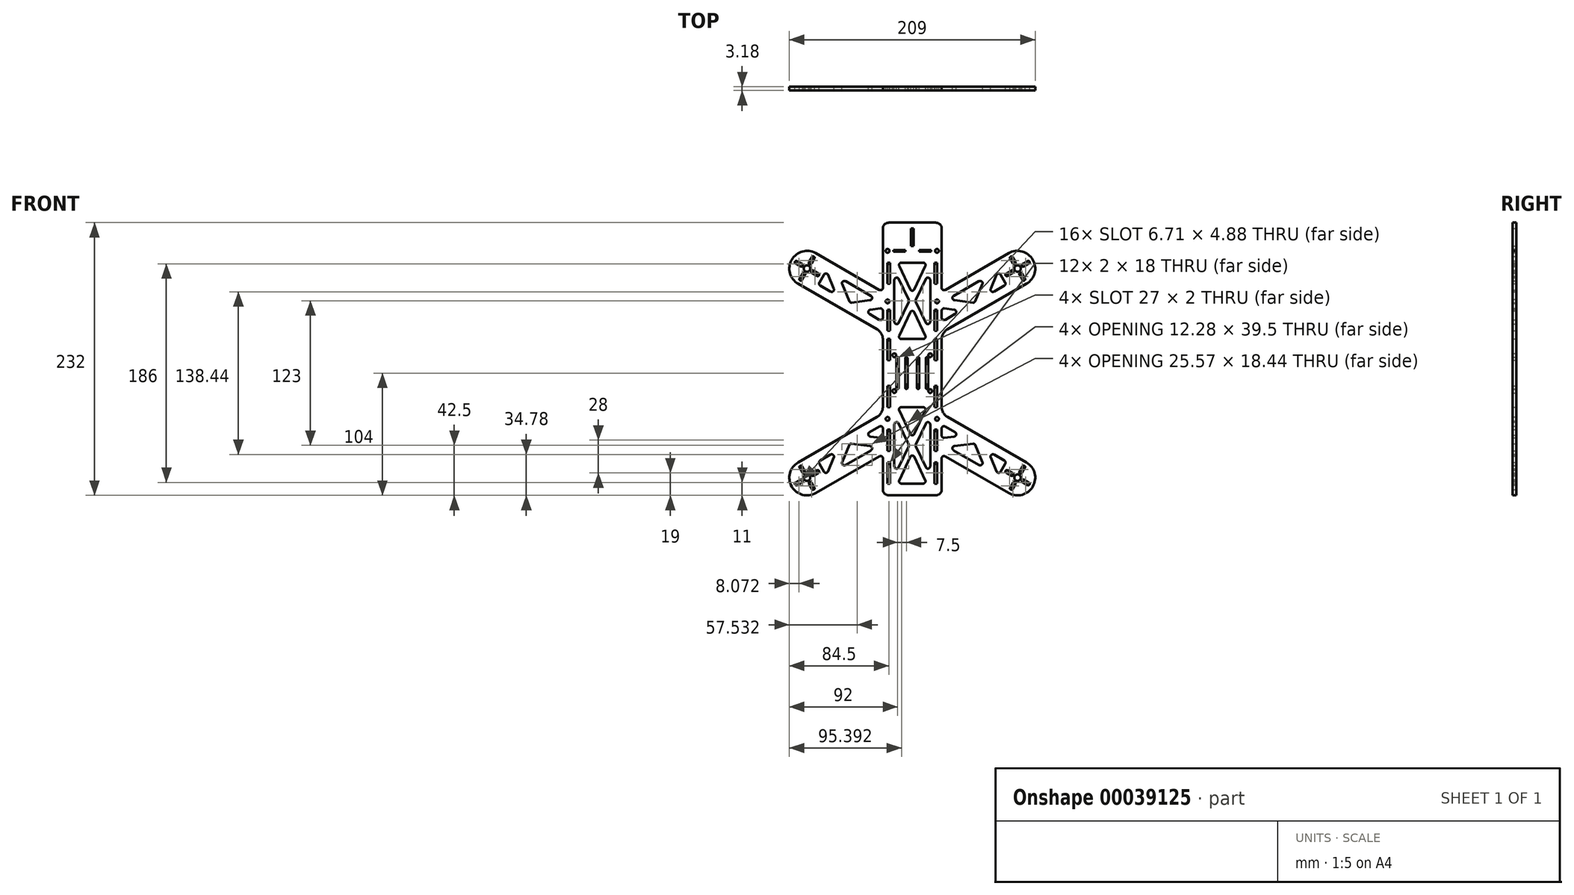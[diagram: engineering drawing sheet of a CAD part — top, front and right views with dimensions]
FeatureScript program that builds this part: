
annotation { "Feature Type Name" : "Feature", "Feature Type Description" : "" }
export const myFeature = defineFeature(function(context is Context, id is Id, definition is map)
    precondition{}
    {
        {
            var Q0;
            Q0=qCreatedBy(makeId("Front.planeOp"),FACE);
            var sketch = newSketch(context, id + "F0", { "sketchPlane" : qUnion([Q0])});
            skArc(sketch, "E0", {"start": v(13.5, 0.5) * mm, "mid": v(12.5, 1.5) * mm, "end": v(11.5, 0.5) * mm});
            skLineSegment(sketch, "E1", {"start": v(13.5, 0.5) * mm, "end": v(13.5, -24.5) * mm});
            skArc(sketch, "E2", {"start": v(11.5, -24.5) * mm, "mid": v(12.5, -25.5) * mm, "end": v(13.5, -24.5) * mm});
            skLineSegment(sketch, "E3", {"start": v(11.5, 0.5) * mm, "end": v(11.5, -24.5) * mm});
            skArc(sketch, "E4", {"start": v(6, 0.5) * mm, "mid": v(5, 1.5) * mm, "end": v(4, 0.5) * mm});
            skLineSegment(sketch, "E5", {"start": v(6, 0.5) * mm, "end": v(6, -24.5) * mm});
            skArc(sketch, "E6", {"start": v(4, -24.5) * mm, "mid": v(5, -25.5) * mm, "end": v(6, -24.5) * mm});
            skLineSegment(sketch, "E7", {"start": v(4, 0.5) * mm, "end": v(4, -24.5) * mm});
            skLineSegment(sketch, "E8", {"start": v(6, 91.25) * mm, "end": v(6, 92.75) * mm});
            skLineSegment(sketch, "E9", {"start": v(6, 92.75) * mm, "end": v(16, 92.75) * mm});
            skLineSegment(sketch, "E10", {"start": v(16, 92.75) * mm, "end": v(16, 91.25) * mm});
            skLineSegment(sketch, "E11", {"start": v(6, 91.25) * mm, "end": v(16, 91.25) * mm});
            skCircle(sketch, "E12", {"center": v(-21, -51) * mm, "radius": 1.6 * mm});
            skCircle(sketch, "E13", {"center": v(-21, 49) * mm, "radius": 1.6 * mm});
            skCircle(sketch, "E14", {"center": v(-21, 92) * mm, "radius": 1.6 * mm});
            skCircle(sketch, "E15", {"center": v(15.25, -27.25) * mm, "radius": 1.6 * mm});
            skCircle(sketch, "E16", {"center": v(-15.25, 3.25) * mm, "radius": 1.6 * mm});
            skCircle(sketch, "E17", {"center": v(-89.5, -101) * mm, "radius": 2.75 * mm});
            skArc(sketch, "E18", {"start": v(-85.34, -97.21) * mm, "mid": v(-85.78, -98.85) * mm, "end": v(-84.14, -99.29) * mm});
            skLineSegment(sketch, "E19", {"start": v(-85.34, -97.21) * mm, "end": v(-81, -94.71) * mm});
            skArc(sketch, "E20", {"start": v(-79.8, -96.79) * mm, "mid": v(-79.37, -95.15) * mm, "end": v(-81, -94.71) * mm});
            skLineSegment(sketch, "E21", {"start": v(-84.14, -99.29) * mm, "end": v(-79.8, -96.79) * mm});
            skArc(sketch, "E22", {"start": v(-85.71, -105.16) * mm, "mid": v(-87.35, -104.72) * mm, "end": v(-87.79, -106.36) * mm});
            skLineSegment(sketch, "E23", {"start": v(-85.71, -105.16) * mm, "end": v(-83.21, -109.5) * mm});
            skArc(sketch, "E24", {"start": v(-85.29, -110.7) * mm, "mid": v(-83.65, -111.13) * mm, "end": v(-83.21, -109.5) * mm});
            skLineSegment(sketch, "E25", {"start": v(-87.79, -106.36) * mm, "end": v(-85.29, -110.7) * mm});
            skArc(sketch, "E26", {"start": v(-93.66, -104.79) * mm, "mid": v(-93.22, -103.15) * mm, "end": v(-94.86, -102.71) * mm});
            skLineSegment(sketch, "E27", {"start": v(-93.66, -104.79) * mm, "end": v(-98, -107.29) * mm});
            skArc(sketch, "E28", {"start": v(-99.2, -105.21) * mm, "mid": v(-99.63, -106.85) * mm, "end": v(-98, -107.29) * mm});
            skLineSegment(sketch, "E29", {"start": v(-94.86, -102.71) * mm, "end": v(-99.2, -105.21) * mm});
            skArc(sketch, "E30", {"start": v(-93.29, -96.84) * mm, "mid": v(-91.65, -97.28) * mm, "end": v(-91.21, -95.64) * mm});
            skLineSegment(sketch, "E31", {"start": v(-93.29, -96.84) * mm, "end": v(-95.79, -92.5) * mm});
            skArc(sketch, "E32", {"start": v(-93.71, -91.3) * mm, "mid": v(-95.35, -90.87) * mm, "end": v(-95.79, -92.5) * mm});
            skLineSegment(sketch, "E33", {"start": v(-91.21, -95.64) * mm, "end": v(-93.71, -91.3) * mm});
            skLineSegment(sketch, "E34", {"start": v(93.66, -104.79) * mm, "end": v(98, -107.29) * mm});
            skArc(sketch, "E35", {"start": v(94.86, -102.71) * mm, "mid": v(93.22, -103.15) * mm, "end": v(93.66, -104.79) * mm});
            skLineSegment(sketch, "E36", {"start": v(94.86, -102.71) * mm, "end": v(99.2, -105.21) * mm});
            skArc(sketch, "E37", {"start": v(98, -107.29) * mm, "mid": v(99.63, -106.85) * mm, "end": v(99.2, -105.21) * mm});
            skLineSegment(sketch, "E38", {"start": v(85.71, -105.16) * mm, "end": v(83.21, -109.5) * mm});
            skArc(sketch, "E39", {"start": v(87.79, -106.36) * mm, "mid": v(87.35, -104.72) * mm, "end": v(85.71, -105.16) * mm});
            skLineSegment(sketch, "E40", {"start": v(87.79, -106.36) * mm, "end": v(85.29, -110.7) * mm});
            skArc(sketch, "E41", {"start": v(83.21, -109.5) * mm, "mid": v(83.65, -111.13) * mm, "end": v(85.29, -110.7) * mm});
            skLineSegment(sketch, "E42", {"start": v(85.34, -97.21) * mm, "end": v(81, -94.71) * mm});
            skArc(sketch, "E43", {"start": v(84.14, -99.29) * mm, "mid": v(85.78, -98.85) * mm, "end": v(85.34, -97.21) * mm});
            skLineSegment(sketch, "E44", {"start": v(84.14, -99.29) * mm, "end": v(79.8, -96.79) * mm});
            skArc(sketch, "E45", {"start": v(81, -94.71) * mm, "mid": v(79.37, -95.15) * mm, "end": v(79.8, -96.79) * mm});
            skLineSegment(sketch, "E46", {"start": v(93.29, -96.84) * mm, "end": v(95.79, -92.5) * mm});
            skArc(sketch, "E47", {"start": v(91.21, -95.64) * mm, "mid": v(91.65, -97.28) * mm, "end": v(93.29, -96.84) * mm});
            skLineSegment(sketch, "E48", {"start": v(91.21, -95.64) * mm, "end": v(93.71, -91.3) * mm});
            skArc(sketch, "E49", {"start": v(95.79, -92.5) * mm, "mid": v(95.35, -90.87) * mm, "end": v(93.71, -91.3) * mm});
            skLineSegment(sketch, "E50", {"start": v(19, 42) * mm, "end": v(19, 24) * mm});
            skLineSegment(sketch, "E51", {"start": v(21, 42) * mm, "end": v(19, 42) * mm});
            skLineSegment(sketch, "E52", {"start": v(21, 42) * mm, "end": v(21, 24) * mm});
            skLineSegment(sketch, "E53", {"start": v(21, 24) * mm, "end": v(19, 24) * mm});
            skLineSegment(sketch, "E54", {"start": v(19, 82) * mm, "end": v(19, 64) * mm});
            skLineSegment(sketch, "E55", {"start": v(21, 82) * mm, "end": v(19, 82) * mm});
            skLineSegment(sketch, "E56", {"start": v(21, 82) * mm, "end": v(21, 64) * mm});
            skLineSegment(sketch, "E57", {"start": v(21, 64) * mm, "end": v(19, 64) * mm});
            skLineSegment(sketch, "E58", {"start": v(-19, -78) * mm, "end": v(-19, -60) * mm});
            skLineSegment(sketch, "E59", {"start": v(-21, -78) * mm, "end": v(-19, -78) * mm});
            skLineSegment(sketch, "E60", {"start": v(-21, -78) * mm, "end": v(-21, -60) * mm});
            skLineSegment(sketch, "E61", {"start": v(-21, -60) * mm, "end": v(-19, -60) * mm});
            skArc(sketch, "E62", {"start": v(-11.44, 68.11) * mm, "mid": v(-13.68, 69.22) * mm, "end": v(-15.25, 67.27) * mm});
            skLineSegment(sketch, "E63", {"start": v(-3.15, 50.35) * mm, "end": v(-11.44, 68.11) * mm});
            skArc(sketch, "E64", {"start": v(-3.15, 48.65) * mm, "mid": v(-2.97, 49.5) * mm, "end": v(-3.15, 50.35) * mm});
            skLineSegment(sketch, "E65", {"start": v(-11.44, 30.89) * mm, "end": v(-3.15, 48.65) * mm});
            skArc(sketch, "E66", {"start": v(-15.25, 31.73) * mm, "mid": v(-13.68, 29.78) * mm, "end": v(-11.44, 30.89) * mm});
            skLineSegment(sketch, "E67", {"start": v(-15.25, 31.73) * mm, "end": v(-15.25, 67.27) * mm});
            skArc(sketch, "E68", {"start": v(-1.81, 59.3) * mm, "mid": v(0, 58.15) * mm, "end": v(1.81, 59.3) * mm});
            skLineSegment(sketch, "E69", {"start": v(-11.07, 79.15) * mm, "end": v(-1.81, 59.3) * mm});
            skArc(sketch, "E70", {"start": v(-9.26, 82) * mm, "mid": v(-10.94, 81.07) * mm, "end": v(-11.07, 79.15) * mm});
            skLineSegment(sketch, "E71", {"start": v(-9.26, 82) * mm, "end": v(9.26, 82) * mm});
            skArc(sketch, "E72", {"start": v(11.07, 79.15) * mm, "mid": v(10.94, 81.07) * mm, "end": v(9.26, 82) * mm});
            skLineSegment(sketch, "E73", {"start": v(1.81, 59.3) * mm, "end": v(11.07, 79.15) * mm});
            skArc(sketch, "E74", {"start": v(11.44, -92.11) * mm, "mid": v(13.68, -93.22) * mm, "end": v(15.25, -91.27) * mm});
            skLineSegment(sketch, "E75", {"start": v(3.15, -74.35) * mm, "end": v(11.44, -92.11) * mm});
            skArc(sketch, "E76", {"start": v(3.15, -72.65) * mm, "mid": v(2.97, -73.5) * mm, "end": v(3.15, -74.35) * mm});
            skLineSegment(sketch, "E77", {"start": v(11.44, -54.89) * mm, "end": v(3.15, -72.65) * mm});
            skArc(sketch, "E78", {"start": v(15.25, -55.73) * mm, "mid": v(13.68, -53.78) * mm, "end": v(11.44, -54.89) * mm});
            skLineSegment(sketch, "E79", {"start": v(15.25, -55.73) * mm, "end": v(15.25, -91.27) * mm});
            skArc(sketch, "E80", {"start": v(-1.81, -63.7) * mm, "mid": v(0, -64.85) * mm, "end": v(1.81, -63.7) * mm});
            skLineSegment(sketch, "E81", {"start": v(-11.07, -43.85) * mm, "end": v(-1.81, -63.7) * mm});
            skArc(sketch, "E82", {"start": v(-9.26, -41) * mm, "mid": v(-10.94, -41.93) * mm, "end": v(-11.07, -43.85) * mm});
            skLineSegment(sketch, "E83", {"start": v(-9.26, -41) * mm, "end": v(9.26, -41) * mm});
            skArc(sketch, "E84", {"start": v(11.07, -43.85) * mm, "mid": v(10.94, -41.93) * mm, "end": v(9.26, -41) * mm});
            skLineSegment(sketch, "E85", {"start": v(1.81, -63.7) * mm, "end": v(11.07, -43.85) * mm});
            skArc(sketch, "E86", {"start": v(-59.6, -87.67) * mm, "mid": v(-59.08, -89.95) * mm, "end": v(-56.76, -90.18) * mm});
            skLineSegment(sketch, "E87", {"start": v(-53.55, -73.23) * mm, "end": v(-59.6, -87.67) * mm});
            skArc(sketch, "E88", {"start": v(-51.46, -72.02) * mm, "mid": v(-52.7, -72.27) * mm, "end": v(-53.55, -73.23) * mm});
            skLineSegment(sketch, "E89", {"start": v(-51.46, -72.02) * mm, "end": v(-35.92, -74) * mm});
            skArc(sketch, "E90", {"start": v(-35.17, -77.72) * mm, "mid": v(-34.21, -75.6) * mm, "end": v(-35.92, -74) * mm});
            skLineSegment(sketch, "E91", {"start": v(-56.76, -90.18) * mm, "end": v(-35.17, -77.72) * mm});
            skArc(sketch, "E92", {"start": v(-78.28, -86.44) * mm, "mid": v(-79.2, -87.65) * mm, "end": v(-79, -89.17) * mm});
            skLineSegment(sketch, "E93", {"start": v(-69.54, -81.4) * mm, "end": v(-78.28, -86.44) * mm});
            skArc(sketch, "E94", {"start": v(-66.7, -83.9) * mm, "mid": v(-67.22, -81.62) * mm, "end": v(-69.54, -81.4) * mm});
            skLineSegment(sketch, "E95", {"start": v(-66.7, -83.9) * mm, "end": v(-71.6, -95.6) * mm});
            skArc(sketch, "E96", {"start": v(-75.17, -95.82) * mm, "mid": v(-73.31, -96.82) * mm, "end": v(-71.6, -95.6) * mm});
            skLineSegment(sketch, "E97", {"start": v(-79, -89.17) * mm, "end": v(-75.17, -95.82) * mm});
            skArc(sketch, "E98", {"start": v(-95.79, 68.5) * mm, "mid": v(-95.35, 66.87) * mm, "end": v(-93.71, 67.3) * mm});
            skLineSegment(sketch, "E99", {"start": v(-93.29, 72.84) * mm, "end": v(-95.79, 68.5) * mm});
            skArc(sketch, "E100", {"start": v(-91.21, 71.64) * mm, "mid": v(-91.65, 73.28) * mm, "end": v(-93.29, 72.84) * mm});
            skLineSegment(sketch, "E101", {"start": v(-91.21, 71.64) * mm, "end": v(-93.71, 67.3) * mm});
            skArc(sketch, "E102", {"start": v(-81, 70.71) * mm, "mid": v(-79.37, 71.15) * mm, "end": v(-79.8, 72.79) * mm});
            skLineSegment(sketch, "E103", {"start": v(-85.34, 73.21) * mm, "end": v(-81, 70.71) * mm});
            skArc(sketch, "E104", {"start": v(-84.14, 75.29) * mm, "mid": v(-85.78, 74.85) * mm, "end": v(-85.34, 73.21) * mm});
            skLineSegment(sketch, "E105", {"start": v(-84.14, 75.29) * mm, "end": v(-79.8, 72.79) * mm});
            skArc(sketch, "E106", {"start": v(-83.21, 85.5) * mm, "mid": v(-83.65, 87.13) * mm, "end": v(-85.29, 86.7) * mm});
            skLineSegment(sketch, "E107", {"start": v(-85.71, 81.16) * mm, "end": v(-83.21, 85.5) * mm});
            skArc(sketch, "E108", {"start": v(-87.79, 82.36) * mm, "mid": v(-87.35, 80.72) * mm, "end": v(-85.71, 81.16) * mm});
            skLineSegment(sketch, "E109", {"start": v(-87.79, 82.36) * mm, "end": v(-85.29, 86.7) * mm});
            skCircle(sketch, "E110", {"center": v(-89.5, 77) * mm, "radius": 2.75 * mm});
            skLineSegment(sketch, "E111", {"start": v(-25, 41.06) * mm, "end": v(-25, 35.14) * mm});
            skArc(sketch, "E112", {"start": v(-28, 33.41) * mm, "mid": v(-26, 33.41) * mm, "end": v(-25, 35.14) * mm});
            skLineSegment(sketch, "E113", {"start": v(-28, 33.41) * mm, "end": v(-36.4, 38.25) * mm});
            skArc(sketch, "E114", {"start": v(-35.64, 41.97) * mm, "mid": v(-37.35, 40.38) * mm, "end": v(-36.4, 38.25) * mm});
            skLineSegment(sketch, "E115", {"start": v(-35.64, 41.97) * mm, "end": v(-27.25, 43.04) * mm});
            skArc(sketch, "E116", {"start": v(-25, 41.06) * mm, "mid": v(-25.68, 42.56) * mm, "end": v(-27.25, 43.04) * mm});
            skArc(sketch, "E117", {"start": v(99.2, 81.21) * mm, "mid": v(99.63, 82.85) * mm, "end": v(98, 83.29) * mm});
            skLineSegment(sketch, "E118", {"start": v(94.86, 78.71) * mm, "end": v(99.2, 81.21) * mm});
            skArc(sketch, "E119", {"start": v(93.66, 80.79) * mm, "mid": v(93.22, 79.15) * mm, "end": v(94.86, 78.71) * mm});
            skLineSegment(sketch, "E120", {"start": v(93.66, 80.79) * mm, "end": v(98, 83.29) * mm});
            skArc(sketch, "E121", {"start": v(79.8, 72.79) * mm, "mid": v(79.37, 71.15) * mm, "end": v(81, 70.71) * mm});
            skLineSegment(sketch, "E122", {"start": v(84.14, 75.29) * mm, "end": v(79.8, 72.79) * mm});
            skArc(sketch, "E123", {"start": v(85.34, 73.21) * mm, "mid": v(85.78, 74.85) * mm, "end": v(84.14, 75.29) * mm});
            skLineSegment(sketch, "E124", {"start": v(85.34, 73.21) * mm, "end": v(81, 70.71) * mm});
            skArc(sketch, "E125", {"start": v(85.29, 86.7) * mm, "mid": v(83.65, 87.13) * mm, "end": v(83.21, 85.5) * mm});
            skLineSegment(sketch, "E126", {"start": v(87.79, 82.36) * mm, "end": v(85.29, 86.7) * mm});
            skArc(sketch, "E127", {"start": v(85.71, 81.16) * mm, "mid": v(87.35, 80.72) * mm, "end": v(87.79, 82.36) * mm});
            skLineSegment(sketch, "E128", {"start": v(85.71, 81.16) * mm, "end": v(83.21, 85.5) * mm});
            skCircle(sketch, "E129", {"center": v(89.5, 77) * mm, "radius": 2.75 * mm});
            skArc(sketch, "E130", {"start": v(93.71, 67.3) * mm, "mid": v(95.35, 66.87) * mm, "end": v(95.79, 68.5) * mm});
            skLineSegment(sketch, "E131", {"start": v(91.21, 71.64) * mm, "end": v(93.71, 67.3) * mm});
            skArc(sketch, "E132", {"start": v(93.29, 72.84) * mm, "mid": v(91.65, 73.28) * mm, "end": v(91.21, 71.64) * mm});
            skLineSegment(sketch, "E133", {"start": v(93.29, 72.84) * mm, "end": v(95.79, 68.5) * mm});
            skArc(sketch, "E134", {"start": v(27.25, 43.04) * mm, "mid": v(25.68, 42.56) * mm, "end": v(25, 41.06) * mm});
            skLineSegment(sketch, "E135", {"start": v(35.64, 41.97) * mm, "end": v(27.25, 43.04) * mm});
            skArc(sketch, "E136", {"start": v(36.4, 38.25) * mm, "mid": v(37.35, 40.38) * mm, "end": v(35.64, 41.97) * mm});
            skLineSegment(sketch, "E137", {"start": v(28, 33.41) * mm, "end": v(36.4, 38.25) * mm});
            skArc(sketch, "E138", {"start": v(25, 35.14) * mm, "mid": v(26, 33.41) * mm, "end": v(28, 33.41) * mm});
            skLineSegment(sketch, "E139", {"start": v(25, 41.06) * mm, "end": v(25, 35.14) * mm});
            skArc(sketch, "E140", {"start": v(75.17, 71.82) * mm, "mid": v(73.31, 72.82) * mm, "end": v(71.6, 71.6) * mm});
            skLineSegment(sketch, "E141", {"start": v(79, 65.17) * mm, "end": v(75.17, 71.82) * mm});
            skArc(sketch, "E142", {"start": v(78.28, 62.44) * mm, "mid": v(79.2, 63.65) * mm, "end": v(79, 65.17) * mm});
            skLineSegment(sketch, "E143", {"start": v(69.54, 57.4) * mm, "end": v(78.28, 62.44) * mm});
            skArc(sketch, "E144", {"start": v(66.7, 59.9) * mm, "mid": v(67.22, 57.62) * mm, "end": v(69.54, 57.4) * mm});
            skLineSegment(sketch, "E145", {"start": v(66.7, 59.9) * mm, "end": v(71.6, 71.6) * mm});
            skArc(sketch, "E146", {"start": v(-28, 58.81) * mm, "mid": v(-26, 58.81) * mm, "end": v(-25, 60.55) * mm});
            skLineSegment(sketch, "E147", {"start": v(-82, 90) * mm, "end": v(-28, 58.81) * mm});
            skArc(sketch, "E148", {"start": v(-82, 90) * mm, "mid": v(-102.5, 84.5) * mm, "end": v(-97, 64) * mm});
            skLineSegment(sketch, "E149", {"start": v(-97, 64) * mm, "end": v(-30, 25.33) * mm});
            skArc(sketch, "E150", {"start": v(-25, 16.67) * mm, "mid": v(-26.34, 21.67) * mm, "end": v(-30, 25.33) * mm});
            skLineSegment(sketch, "E151", {"start": v(-25, -40.67) * mm, "end": v(-25, 16.67) * mm});
            skArc(sketch, "E152", {"start": v(-30, -49.33) * mm, "mid": v(-26.34, -45.67) * mm, "end": v(-25, -40.67) * mm});
            skLineSegment(sketch, "E153", {"start": v(-97, -88) * mm, "end": v(-30, -49.33) * mm});
            skArc(sketch, "E154", {"start": v(-97, -88) * mm, "mid": v(-102.5, -108.5) * mm, "end": v(-82, -114) * mm});
            skLineSegment(sketch, "E155", {"start": v(-82, -114) * mm, "end": v(-28, -82.81) * mm});
            skArc(sketch, "E156", {"start": v(-25, -84.55) * mm, "mid": v(-26, -82.81) * mm, "end": v(-28, -82.81) * mm});
            skLineSegment(sketch, "E157", {"start": v(-25, -111) * mm, "end": v(-25, -84.55) * mm});
            skArc(sketch, "E158", {"start": v(-25, -111) * mm, "mid": v(-23.54, -114.54) * mm, "end": v(-20, -116) * mm});
            skLineSegment(sketch, "E159", {"start": v(-20, -116) * mm, "end": v(20, -116) * mm});
            skArc(sketch, "E160", {"start": v(20, -116) * mm, "mid": v(23.54, -114.54) * mm, "end": v(25, -111) * mm});
            skLineSegment(sketch, "E161", {"start": v(25, -111) * mm, "end": v(25, -84.55) * mm});
            skArc(sketch, "E162", {"start": v(28, -82.81) * mm, "mid": v(26, -82.81) * mm, "end": v(25, -84.55) * mm});
            skLineSegment(sketch, "E163", {"start": v(82, -114) * mm, "end": v(28, -82.81) * mm});
            skArc(sketch, "E164", {"start": v(82, -114) * mm, "mid": v(102.5, -108.5) * mm, "end": v(97, -88) * mm});
            skLineSegment(sketch, "E165", {"start": v(97, -88) * mm, "end": v(30, -49.33) * mm});
            skArc(sketch, "E166", {"start": v(25, -40.67) * mm, "mid": v(26.34, -45.67) * mm, "end": v(30, -49.33) * mm});
            skLineSegment(sketch, "E167", {"start": v(25, -40.67) * mm, "end": v(25, 16.67) * mm});
            skArc(sketch, "E168", {"start": v(30, 25.33) * mm, "mid": v(26.34, 21.67) * mm, "end": v(25, 16.67) * mm});
            skLineSegment(sketch, "E169", {"start": v(97, 64) * mm, "end": v(30, 25.33) * mm});
            skArc(sketch, "E170", {"start": v(97, 64) * mm, "mid": v(102.5, 84.5) * mm, "end": v(82, 90) * mm});
            skLineSegment(sketch, "E171", {"start": v(82, 90) * mm, "end": v(28, 58.81) * mm});
            skArc(sketch, "E172", {"start": v(25, 60.55) * mm, "mid": v(26, 58.81) * mm, "end": v(28, 58.81) * mm});
            skLineSegment(sketch, "E173", {"start": v(25, 60.55) * mm, "end": v(25, 111) * mm});
            skArc(sketch, "E174", {"start": v(25, 111) * mm, "mid": v(23.54, 114.54) * mm, "end": v(20, 116) * mm});
            skLineSegment(sketch, "E175", {"start": v(-20, 116) * mm, "end": v(20, 116) * mm});
            skArc(sketch, "E176", {"start": v(-20, 116) * mm, "mid": v(-23.54, 114.54) * mm, "end": v(-25, 111) * mm});
            skLineSegment(sketch, "E177", {"start": v(-25, 60.55) * mm, "end": v(-25, 111) * mm});
            skArc(sketch, "E178", {"start": v(59.6, 63.67) * mm, "mid": v(59.08, 65.95) * mm, "end": v(56.76, 66.18) * mm});
            skLineSegment(sketch, "E179", {"start": v(53.55, 49.23) * mm, "end": v(59.6, 63.67) * mm});
            skArc(sketch, "E180", {"start": v(51.46, 48.02) * mm, "mid": v(52.7, 48.27) * mm, "end": v(53.55, 49.23) * mm});
            skLineSegment(sketch, "E181", {"start": v(51.46, 48.02) * mm, "end": v(35.92, 50) * mm});
            skArc(sketch, "E182", {"start": v(35.17, 53.72) * mm, "mid": v(34.21, 51.6) * mm, "end": v(35.92, 50) * mm});
            skLineSegment(sketch, "E183", {"start": v(56.76, 66.18) * mm, "end": v(35.17, 53.72) * mm});
            skArc(sketch, "E184", {"start": v(-35.92, 50) * mm, "mid": v(-34.21, 51.6) * mm, "end": v(-35.17, 53.72) * mm});
            skLineSegment(sketch, "E185", {"start": v(-51.46, 48.02) * mm, "end": v(-35.92, 50) * mm});
            skArc(sketch, "E186", {"start": v(-53.55, 49.23) * mm, "mid": v(-52.7, 48.27) * mm, "end": v(-51.46, 48.02) * mm});
            skLineSegment(sketch, "E187", {"start": v(-53.55, 49.23) * mm, "end": v(-59.6, 63.67) * mm});
            skArc(sketch, "E188", {"start": v(-56.76, 66.18) * mm, "mid": v(-59.08, 65.95) * mm, "end": v(-59.6, 63.67) * mm});
            skLineSegment(sketch, "E189", {"start": v(-56.76, 66.18) * mm, "end": v(-35.17, 53.72) * mm});
            skArc(sketch, "E190", {"start": v(-71.6, 71.6) * mm, "mid": v(-73.31, 72.82) * mm, "end": v(-75.17, 71.82) * mm});
            skLineSegment(sketch, "E191", {"start": v(-66.7, 59.9) * mm, "end": v(-71.6, 71.6) * mm});
            skArc(sketch, "E192", {"start": v(-69.54, 57.4) * mm, "mid": v(-67.22, 57.62) * mm, "end": v(-66.7, 59.9) * mm});
            skLineSegment(sketch, "E193", {"start": v(-69.54, 57.4) * mm, "end": v(-78.28, 62.44) * mm});
            skArc(sketch, "E194", {"start": v(-79, 65.17) * mm, "mid": v(-79.2, 63.65) * mm, "end": v(-78.28, 62.44) * mm});
            skLineSegment(sketch, "E195", {"start": v(-79, 65.17) * mm, "end": v(-75.17, 71.82) * mm});
            skArc(sketch, "E196", {"start": v(-98, 83.29) * mm, "mid": v(-99.63, 82.85) * mm, "end": v(-99.2, 81.21) * mm});
            skLineSegment(sketch, "E197", {"start": v(-93.66, 80.79) * mm, "end": v(-98, 83.29) * mm});
            skArc(sketch, "E198", {"start": v(-94.86, 78.71) * mm, "mid": v(-93.22, 79.15) * mm, "end": v(-93.66, 80.79) * mm});
            skLineSegment(sketch, "E199", {"start": v(-94.86, 78.71) * mm, "end": v(-99.2, 81.21) * mm});
            skLineSegment(sketch, "E200", {"start": v(35.64, -65.97) * mm, "end": v(27.25, -67.04) * mm});
            skArc(sketch, "E201", {"start": v(25, -65.06) * mm, "mid": v(25.68, -66.56) * mm, "end": v(27.25, -67.04) * mm});
            skLineSegment(sketch, "E202", {"start": v(25, -65.06) * mm, "end": v(25, -59.14) * mm});
            skArc(sketch, "E203", {"start": v(28, -57.41) * mm, "mid": v(26, -57.41) * mm, "end": v(25, -59.14) * mm});
            skLineSegment(sketch, "E204", {"start": v(28, -57.41) * mm, "end": v(36.4, -62.25) * mm});
            skArc(sketch, "E205", {"start": v(35.64, -65.97) * mm, "mid": v(37.35, -64.38) * mm, "end": v(36.4, -62.25) * mm});
            skArc(sketch, "E206", {"start": v(56.76, -90.18) * mm, "mid": v(59.08, -89.95) * mm, "end": v(59.6, -87.67) * mm});
            skLineSegment(sketch, "E207", {"start": v(56.76, -90.18) * mm, "end": v(35.17, -77.72) * mm});
            skArc(sketch, "E208", {"start": v(35.92, -74) * mm, "mid": v(34.21, -75.6) * mm, "end": v(35.17, -77.72) * mm});
            skLineSegment(sketch, "E209", {"start": v(51.46, -72.02) * mm, "end": v(35.92, -74) * mm});
            skArc(sketch, "E210", {"start": v(53.55, -73.23) * mm, "mid": v(52.7, -72.27) * mm, "end": v(51.46, -72.02) * mm});
            skLineSegment(sketch, "E211", {"start": v(53.55, -73.23) * mm, "end": v(59.6, -87.67) * mm});
            skArc(sketch, "E212", {"start": v(79, -89.17) * mm, "mid": v(79.2, -87.65) * mm, "end": v(78.28, -86.44) * mm});
            skLineSegment(sketch, "E213", {"start": v(79, -89.17) * mm, "end": v(75.17, -95.82) * mm});
            skArc(sketch, "E214", {"start": v(71.6, -95.6) * mm, "mid": v(73.31, -96.82) * mm, "end": v(75.17, -95.82) * mm});
            skLineSegment(sketch, "E215", {"start": v(66.7, -83.9) * mm, "end": v(71.6, -95.6) * mm});
            skArc(sketch, "E216", {"start": v(69.54, -81.4) * mm, "mid": v(67.22, -81.62) * mm, "end": v(66.7, -83.9) * mm});
            skLineSegment(sketch, "E217", {"start": v(69.54, -81.4) * mm, "end": v(78.28, -86.44) * mm});
            skArc(sketch, "E218", {"start": v(-36.4, -62.25) * mm, "mid": v(-37.35, -64.38) * mm, "end": v(-35.64, -65.97) * mm});
            skLineSegment(sketch, "E219", {"start": v(-28, -57.41) * mm, "end": v(-36.4, -62.25) * mm});
            skArc(sketch, "E220", {"start": v(-25, -59.14) * mm, "mid": v(-26, -57.41) * mm, "end": v(-28, -57.41) * mm});
            skLineSegment(sketch, "E221", {"start": v(-25, -65.06) * mm, "end": v(-25, -59.14) * mm});
            skArc(sketch, "E222", {"start": v(-27.25, -67.04) * mm, "mid": v(-25.68, -66.56) * mm, "end": v(-25, -65.06) * mm});
            skLineSegment(sketch, "E223", {"start": v(-35.64, -65.97) * mm, "end": v(-27.25, -67.04) * mm});
            skArc(sketch, "E224", {"start": v(-15.25, -91.27) * mm, "mid": v(-13.68, -93.22) * mm, "end": v(-11.44, -92.11) * mm});
            skLineSegment(sketch, "E225", {"start": v(-15.25, -55.73) * mm, "end": v(-15.25, -91.27) * mm});
            skArc(sketch, "E226", {"start": v(-11.44, -54.89) * mm, "mid": v(-13.68, -53.78) * mm, "end": v(-15.25, -55.73) * mm});
            skLineSegment(sketch, "E227", {"start": v(-11.44, -54.89) * mm, "end": v(-3.15, -72.65) * mm});
            skArc(sketch, "E228", {"start": v(-3.15, -74.35) * mm, "mid": v(-2.97, -73.5) * mm, "end": v(-3.15, -72.65) * mm});
            skLineSegment(sketch, "E229", {"start": v(-3.15, -74.35) * mm, "end": v(-11.44, -92.11) * mm});
            skLineSegment(sketch, "E230", {"start": v(-11.07, -103.15) * mm, "end": v(-1.81, -83.3) * mm});
            skArc(sketch, "E231", {"start": v(1.81, -83.3) * mm, "mid": v(0, -82.15) * mm, "end": v(-1.81, -83.3) * mm});
            skLineSegment(sketch, "E232", {"start": v(1.81, -83.3) * mm, "end": v(11.07, -103.15) * mm});
            skArc(sketch, "E233", {"start": v(9.26, -106) * mm, "mid": v(10.94, -105.07) * mm, "end": v(11.07, -103.15) * mm});
            skLineSegment(sketch, "E234", {"start": v(-9.26, -106) * mm, "end": v(9.26, -106) * mm});
            skArc(sketch, "E235", {"start": v(-11.07, -103.15) * mm, "mid": v(-10.94, -105.07) * mm, "end": v(-9.26, -106) * mm});
            skLineSegment(sketch, "E236", {"start": v(-11.07, 19.85) * mm, "end": v(-1.81, 39.7) * mm});
            skArc(sketch, "E237", {"start": v(1.81, 39.7) * mm, "mid": v(0, 40.85) * mm, "end": v(-1.81, 39.7) * mm});
            skLineSegment(sketch, "E238", {"start": v(1.81, 39.7) * mm, "end": v(11.07, 19.85) * mm});
            skArc(sketch, "E239", {"start": v(9.26, 17) * mm, "mid": v(10.94, 17.93) * mm, "end": v(11.07, 19.85) * mm});
            skLineSegment(sketch, "E240", {"start": v(-9.26, 17) * mm, "end": v(9.26, 17) * mm});
            skArc(sketch, "E241", {"start": v(-11.07, 19.85) * mm, "mid": v(-10.94, 17.93) * mm, "end": v(-9.26, 17) * mm});
            skLineSegment(sketch, "E242", {"start": v(-19, -23) * mm, "end": v(-19, -41) * mm});
            skLineSegment(sketch, "E243", {"start": v(-21, -41) * mm, "end": v(-19, -41) * mm});
            skLineSegment(sketch, "E244", {"start": v(-21, -23) * mm, "end": v(-21, -41) * mm});
            skLineSegment(sketch, "E245", {"start": v(-21, -23) * mm, "end": v(-19, -23) * mm});
            skLineSegment(sketch, "E246", {"start": v(21, 17) * mm, "end": v(21, -1) * mm});
            skLineSegment(sketch, "E247", {"start": v(21, -1) * mm, "end": v(19, -1) * mm});
            skLineSegment(sketch, "E248", {"start": v(19, 17) * mm, "end": v(19, -1) * mm});
            skLineSegment(sketch, "E249", {"start": v(21, 17) * mm, "end": v(19, 17) * mm});
            skLineSegment(sketch, "E250", {"start": v(-19, 17) * mm, "end": v(-19, -1) * mm});
            skLineSegment(sketch, "E251", {"start": v(-21, -1) * mm, "end": v(-19, -1) * mm});
            skLineSegment(sketch, "E252", {"start": v(-21, 17) * mm, "end": v(-21, -1) * mm});
            skLineSegment(sketch, "E253", {"start": v(-21, 17) * mm, "end": v(-19, 17) * mm});
            skLineSegment(sketch, "E254", {"start": v(19, -106) * mm, "end": v(19, -88) * mm});
            skLineSegment(sketch, "E255", {"start": v(19, -88) * mm, "end": v(21, -88) * mm});
            skLineSegment(sketch, "E256", {"start": v(21, -106) * mm, "end": v(21, -88) * mm});
            skLineSegment(sketch, "E257", {"start": v(19, -106) * mm, "end": v(21, -106) * mm});
            skLineSegment(sketch, "E258", {"start": v(21, -78) * mm, "end": v(19, -78) * mm});
            skLineSegment(sketch, "E259", {"start": v(19, -78) * mm, "end": v(19, -60) * mm});
            skLineSegment(sketch, "E260", {"start": v(21, -60) * mm, "end": v(19, -60) * mm});
            skLineSegment(sketch, "E261", {"start": v(21, -78) * mm, "end": v(21, -60) * mm});
            skLineSegment(sketch, "E262", {"start": v(-21, -106) * mm, "end": v(-21, -88) * mm});
            skLineSegment(sketch, "E263", {"start": v(-19, -88) * mm, "end": v(-21, -88) * mm});
            skLineSegment(sketch, "E264", {"start": v(-19, -106) * mm, "end": v(-19, -88) * mm});
            skLineSegment(sketch, "E265", {"start": v(-19, -106) * mm, "end": v(-21, -106) * mm});
            skLineSegment(sketch, "E266", {"start": v(-19, 42) * mm, "end": v(-19, 24) * mm});
            skLineSegment(sketch, "E267", {"start": v(-21, 24) * mm, "end": v(-19, 24) * mm});
            skLineSegment(sketch, "E268", {"start": v(-21, 42) * mm, "end": v(-21, 24) * mm});
            skLineSegment(sketch, "E269", {"start": v(-21, 42) * mm, "end": v(-19, 42) * mm});
            skLineSegment(sketch, "E270", {"start": v(-19, 82) * mm, "end": v(-19, 64) * mm});
            skLineSegment(sketch, "E271", {"start": v(-21, 64) * mm, "end": v(-19, 64) * mm});
            skLineSegment(sketch, "E272", {"start": v(-21, 82) * mm, "end": v(-21, 64) * mm});
            skLineSegment(sketch, "E273", {"start": v(-21, 82) * mm, "end": v(-19, 82) * mm});
            skCircle(sketch, "E274", {"center": v(89.5, -101) * mm, "radius": 2.75 * mm});
            skCircle(sketch, "E275", {"center": v(15.25, 3.25) * mm, "radius": 1.6 * mm});
            skCircle(sketch, "E276", {"center": v(-15.25, -27.25) * mm, "radius": 1.6 * mm});
            skCircle(sketch, "E277", {"center": v(21, 92) * mm, "radius": 1.6 * mm});
            skCircle(sketch, "E278", {"center": v(21, 49) * mm, "radius": 1.6 * mm});
            skCircle(sketch, "E279", {"center": v(21, -51) * mm, "radius": 1.6 * mm});
            skLineSegment(sketch, "E280", {"start": v(15.25, 31.73) * mm, "end": v(15.25, 67.27) * mm});
            skArc(sketch, "E281", {"start": v(11.44, 30.89) * mm, "mid": v(13.68, 29.78) * mm, "end": v(15.25, 31.73) * mm});
            skLineSegment(sketch, "E282", {"start": v(11.44, 30.89) * mm, "end": v(3.15, 48.65) * mm});
            skArc(sketch, "E283", {"start": v(3.15, 50.35) * mm, "mid": v(2.97, 49.5) * mm, "end": v(3.15, 48.65) * mm});
            skLineSegment(sketch, "E284", {"start": v(3.15, 50.35) * mm, "end": v(11.44, 68.11) * mm});
            skArc(sketch, "E285", {"start": v(15.25, 67.27) * mm, "mid": v(13.68, 69.22) * mm, "end": v(11.44, 68.11) * mm});
            skLineSegment(sketch, "E286", {"start": v(-16, 91.25) * mm, "end": v(-6, 91.25) * mm});
            skLineSegment(sketch, "E287", {"start": v(-16, 92.75) * mm, "end": v(-16, 91.25) * mm});
            skLineSegment(sketch, "E288", {"start": v(-16, 92.75) * mm, "end": v(-6, 92.75) * mm});
            skLineSegment(sketch, "E289", {"start": v(-6, 91.25) * mm, "end": v(-6, 92.75) * mm});
            skLineSegment(sketch, "E290", {"start": v(-1, 96) * mm, "end": v(1, 96) * mm});
            skLineSegment(sketch, "E291", {"start": v(-1, 111) * mm, "end": v(-1, 96) * mm});
            skLineSegment(sketch, "E292", {"start": v(-1, 111) * mm, "end": v(1, 111) * mm});
            skLineSegment(sketch, "E293", {"start": v(1, 111) * mm, "end": v(1, 96) * mm});
            skLineSegment(sketch, "E294", {"start": v(-13.5, 0.5) * mm, "end": v(-13.5, -24.5) * mm});
            skArc(sketch, "E295", {"start": v(-11.5, 0.5) * mm, "mid": v(-12.5, 1.5) * mm, "end": v(-13.5, 0.5) * mm});
            skLineSegment(sketch, "E296", {"start": v(-11.5, 0.5) * mm, "end": v(-11.5, -24.5) * mm});
            skArc(sketch, "E297", {"start": v(-13.5, -24.5) * mm, "mid": v(-12.5, -25.5) * mm, "end": v(-11.5, -24.5) * mm});
            skLineSegment(sketch, "E298", {"start": v(-6, 0.5) * mm, "end": v(-6, -24.5) * mm});
            skArc(sketch, "E299", {"start": v(-4, 0.5) * mm, "mid": v(-5, 1.5) * mm, "end": v(-6, 0.5) * mm});
            skLineSegment(sketch, "E300", {"start": v(-4, 0.5) * mm, "end": v(-4, -24.5) * mm});
            skArc(sketch, "E301", {"start": v(-6, -24.5) * mm, "mid": v(-5, -25.5) * mm, "end": v(-4, -24.5) * mm});
            skLineSegment(sketch, "E302", {"start": v(19, -23) * mm, "end": v(19, -41) * mm});
            skLineSegment(sketch, "E303", {"start": v(21, -23) * mm, "end": v(19, -23) * mm});
            skLineSegment(sketch, "E304", {"start": v(21, -23) * mm, "end": v(21, -41) * mm});
            skLineSegment(sketch, "E305", {"start": v(21, -41) * mm, "end": v(19, -41) * mm});
            skSolve(sketch);
        }
        {
            var Q0;
            Q0 = qSketchRegion(id + "F0", true);
            extrude(context, id + "F1", {"entities" : qUnion([Q0]), "depth" : 3.17 * mm});
        }
    });
